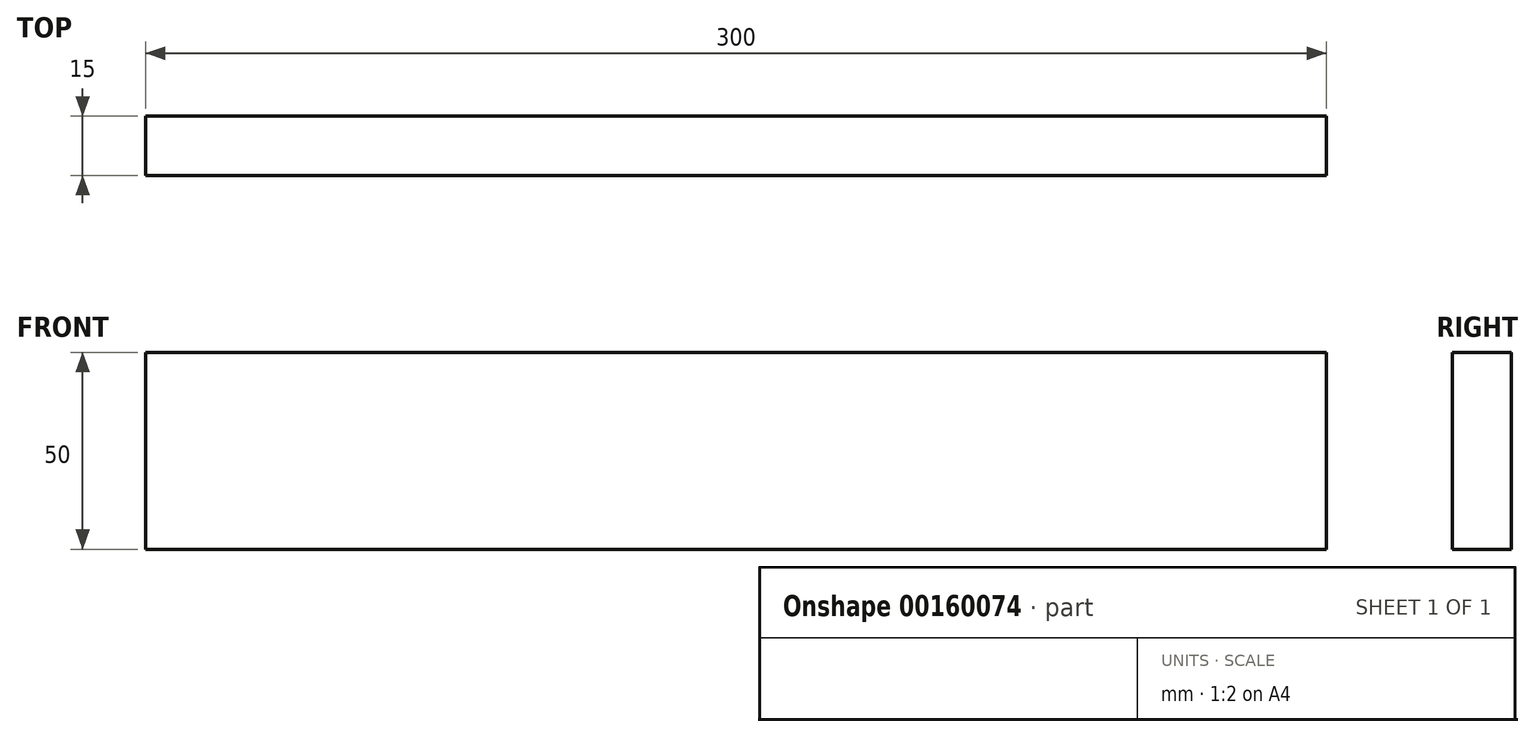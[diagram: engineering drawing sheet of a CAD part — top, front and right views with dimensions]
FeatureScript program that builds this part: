
annotation { "Feature Type Name" : "Feature", "Feature Type Description" : "" }
export const myFeature = defineFeature(function(context is Context, id is Id, definition is map)
    precondition{}
    {
        {
            var Q0;
            Q0=qCreatedBy(makeId("Front.planeOp"),FACE);
            var sketch = newSketch(context, id + "F0", { "sketchPlane" : qUnion([Q0])});
            skLineSegment(sketch, "E0.bottom", {"start": v(0, 0) * mm, "end": v(300, 0) * mm});
            skLineSegment(sketch, "E0.top", {"start": v(0, 50) * mm, "end": v(300, 50) * mm});
            skLineSegment(sketch, "E0.left", {"start": v(0, 0) * mm, "end": v(0, 50) * mm});
            skLineSegment(sketch, "E0.right", {"start": v(300, 0) * mm, "end": v(300, 50) * mm});
            skSolve(sketch);
        }
        {
            var Q0;
            Q0=makeQuery(id+"F0.imprint","IMPRINT",FACE,{"disambiguationData":[TD([[makeQuery(id+"F0.imprint","IMPRINT",EDGE,{"derivedFrom":sQuery(id+"F0.wireOp",EDGE,"E0.bottom")}),1.0]])]});
            extrude(context, id + "F1", {"entities" : qUnion([Q0]), "depth" : 15 * mm});
        }
    });
